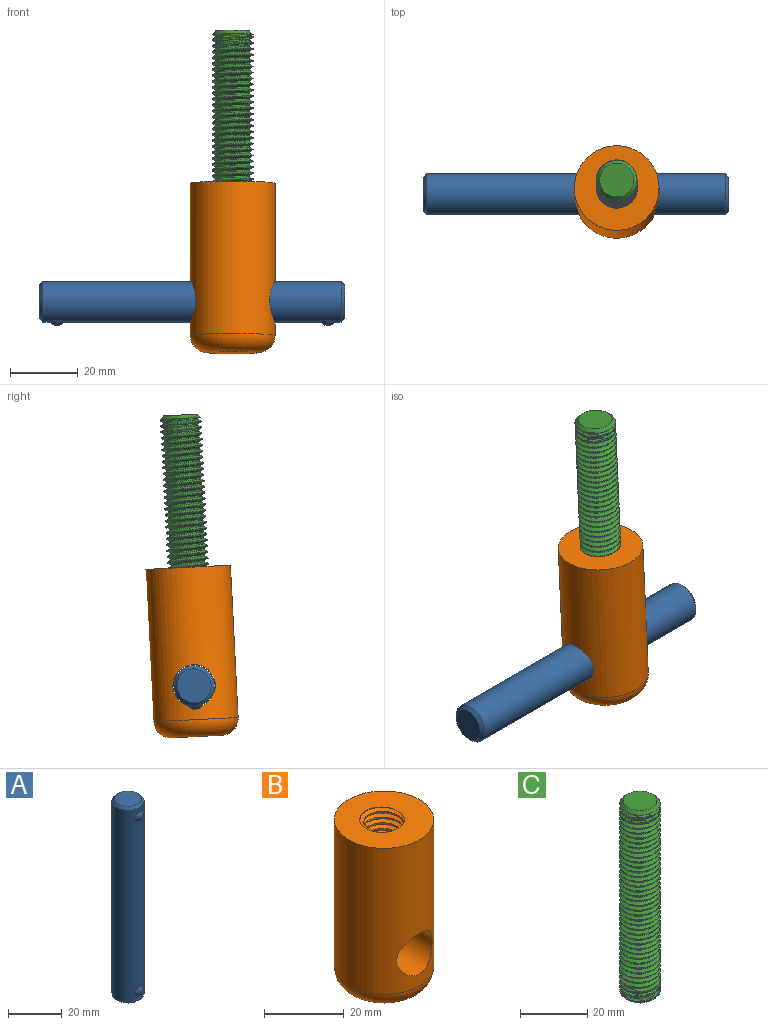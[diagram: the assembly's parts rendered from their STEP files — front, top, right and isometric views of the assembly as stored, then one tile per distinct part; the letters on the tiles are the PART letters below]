
ASSEMBLY  parts=3 mates=2
PART A: 7 faces, bbox 12x13x90 mm
  f0: cylinder r=6mm len=88mm, axis (0,0,-1), area 3288.4mm2, adj f3,f4,f5,f6
  f1: plane 10x10mm, normal (0,0,1), area 78.5mm2, adj f3
  f2: plane 10x10mm, normal (0,0,-1), area 78.5mm2, adj f4
  f3: cone r=5mm half-angle=45deg, axis (0,0,-1), area 48.9mm2, adj f0,f1
  f4: cone r=6mm half-angle=45deg, axis (0,0,1), area 48.9mm2, adj f0,f2
  f5: sphere r=2.5mm, area 19mm2, adj f0
  f6: sphere r=2.5mm, area 19mm2, adj f0
PART B: 12 faces, bbox 27.6x27.6x51.2 mm
  f0: cylinder r=12.5mm len=45mm, axis (0,0,-1), area 3280.2mm2, adj f1,f10,f11
  f1: plane 25.52x25.52mm, normal (0,0,1), area 393.9mm2, adj f0,f4,f5,f6,f9
  f2: plane 15x15mm, normal (0,0,-1), area 176.7mm2, adj f11
  f3: cone r=0mm half-angle=59deg, axis (0,0,1), area 131.9mm2, adj f7,f8
  f4: bspline ~26.21x14.02mm, area 549.6mm2, adj f1,f6,f7,f8,f9
  f5: bspline ~26.51x14.02mm, area 550.6mm2, adj f1,f6,f7,f8,f9
  f6: bspline ~25.59x14.21mm, area 138.4mm2, adj f1,f4,f5,f7
  f7: plane 5.29x3.38mm, normal (0,0,1), area 0.6mm2, adj f3,f4,f5,f6
  f8: plane 12.43x12.43mm, normal (0,0,-1), area 16.7mm2, adj f3,f4,f5,f9
  f9: cylinder r=5.12mm len=25mm, axis (0,0,-1), area 225mm2, adj f1,f4,f5,f8
  f10: cylinder r=6.25mm len=25mm, axis (0,-1,0), area 917.2mm2, adj f0
  f11: torus R=7.5mm, axis (0,0,1), area 527.2mm2, adj f0,f2
PART C: 10 faces, bbox 12.5x14.3x70.5 mm
  f0: cylinder r=6mm len=68mm, axis (0,0,-1), area 754.3mm2, adj f3,f4,f6,f7
  f1: plane 10x10mm, normal (0,0,1), area 78.5mm2, adj f4
  f2: plane 10x10mm, normal (0,0,-1), area 78.5mm2, adj f3
  f3: cone r=6mm half-angle=45deg, axis (0,0,1), area 48.9mm2, adj f0,f2,f9
  f4: cone r=5mm half-angle=45deg, axis (0,0,-1), area 48.9mm2, adj f0,f1,f8
  f5: bspline ~69.27x11.67mm, area 596.3mm2, adj f6,f7,f8,f9
  f6: bspline ~69.38x13.86mm, area 1480.4mm2, adj f0,f5,f8,f9
  f7: bspline ~69.38x13.86mm, area 1479.7mm2, adj f0,f5,f8,f9
  f8: plane 12.48x12.48mm, normal (0,0,-1), area 19.3mm2, adj f4,f5,f6,f7
  f9: plane 12.49x12.49mm, normal (0,0,1), area 19.3mm2, adj f3,f5,f6,f7
PLACE A rot(axis=(0.57,-0.6,-0.57),118.3deg) t=(107.99,-47.99,45.52)mm fixed
PLACE B rot(axis=(-0.03,-0.03,-1),90deg) t=(75,-48.74,30.54)mm fixed
PLACE C rot(axis=(1,0,0),177.1deg) t=(75,-43.97,125.42)mm
MATE slider A.f0 <-> B.f10  axis (1,0,0) through (62.99,-47.99,45.52)mm
MATE fastened C.f0 <-> B.f0  axis (0,0.05,1) through (75,-43.97,125.42)mm
